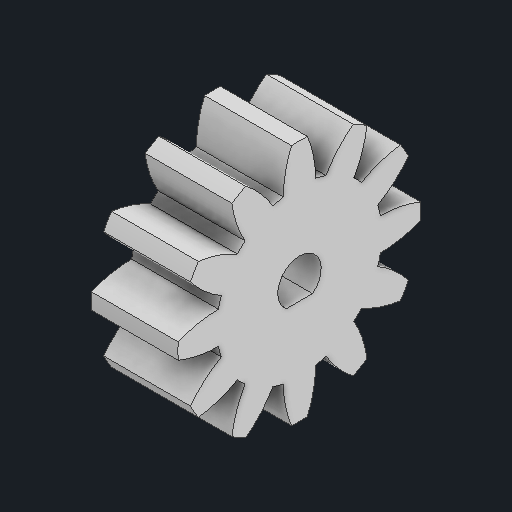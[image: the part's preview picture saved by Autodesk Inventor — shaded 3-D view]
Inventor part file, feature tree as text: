
AUTODESK INVENTOR PART (.ipt)
format: ipt  version: 2022 (Build 260153000, 153)  size: 228,864 bytes
history: native  units: mm
features: extrude x4, sketch x4, other x3
ambient origin geometry x8: Origin, YZ Plane, XZ Plane, XY Plane, X Axis, Y Axis, Z Axis, Center Point
bodies: Solid1 (feature_tree)
feature tree (11):
  other  "{BB8FE430-83BF-418D-8DF9-9B323D3DB9B9}"
  extrude  "Extrusion1"  Depth=16.0mm TaperAngle=0.0deg
  extrude  "Extrusion2"  Depth=3.0mm
  extrude  "Extrusion3"  TaperAngle=0.0deg  [1 undecoded]
  extrude  "Extrusion4"  Depth=30.0mm
  other  "Spur Gear Teeth2"
  sketch  "Sketch1"  dims[d0=36.0mm d1=16.0mm d2=0.0mm]
  sketch  "Sketch2"  dims[d3=5.0mm d7=3.0mm]
  sketch  "Sketch3"  dims[d8=2.0mm d9=0.0mm d10=0.0mm]
  sketch  "Sketch4"  dims[d11=6.0mm d12=0.0mm d13=30.0mm d14=36.0mm d15=6.0mm d16=0.0mm]
  other  "Spur Gear1"
note: 1 required parameter value undecoded (feature->parameter linkage not recoverable at this tier; creation-order binding heuristic only, values carry confidence <= 0.55)
